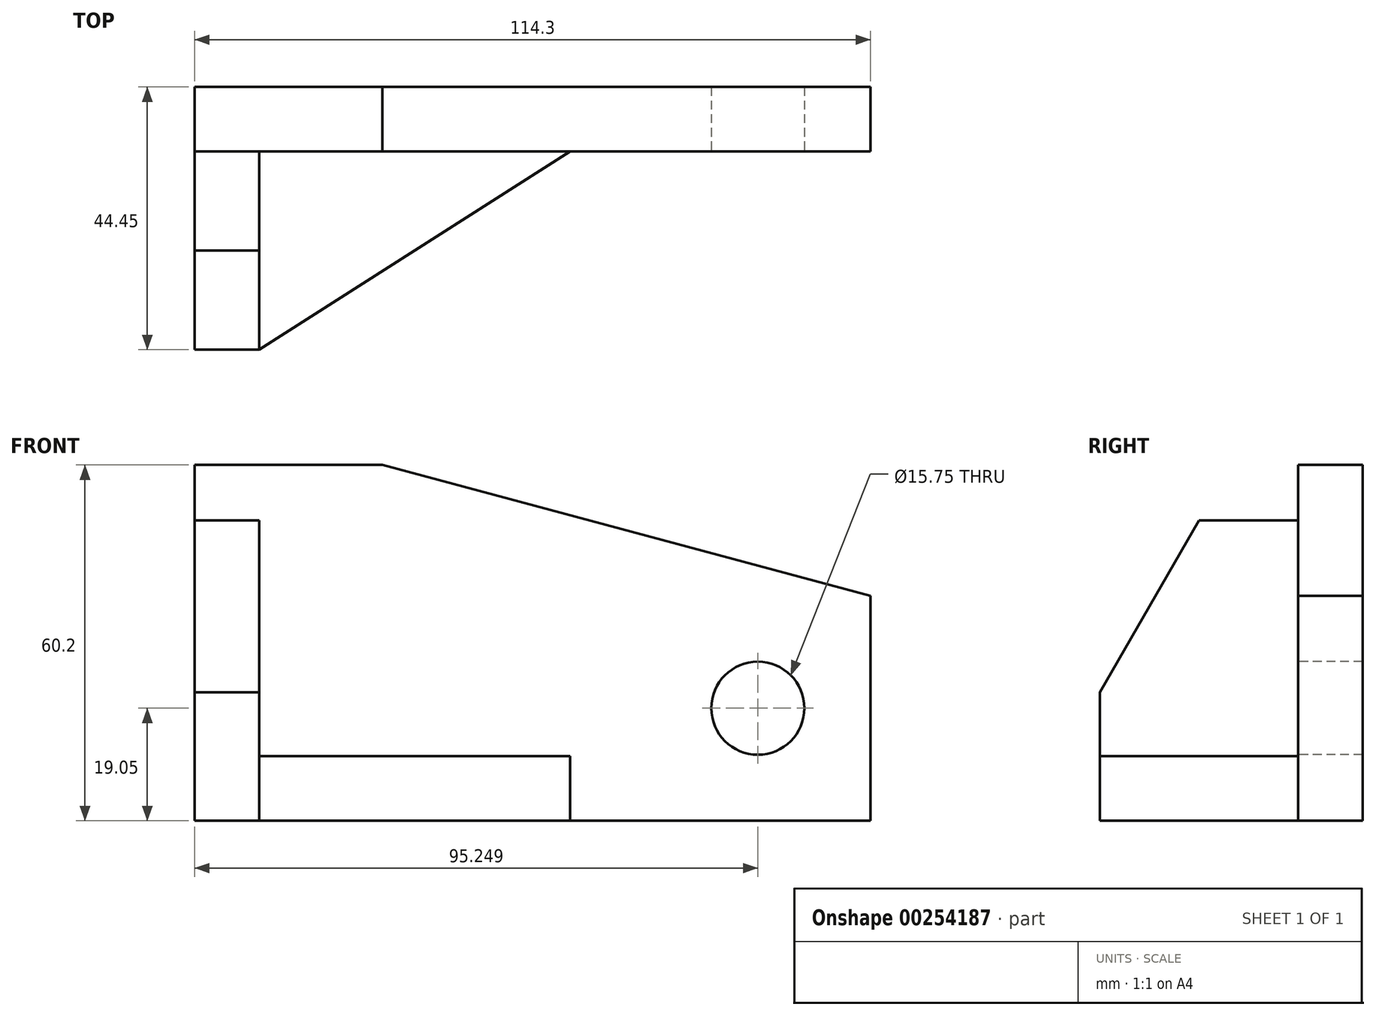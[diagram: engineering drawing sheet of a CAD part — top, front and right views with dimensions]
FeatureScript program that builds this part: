
annotation { "Feature Type Name" : "Feature", "Feature Type Description" : "" }
export const myFeature = defineFeature(function(context is Context, id is Id, definition is map)
    precondition{}
    {
        {
            var Q0;
            Q0=qCreatedBy(makeId("Top.planeOp"),FACE);
            var sketch = newSketch(context, id + "F0", { "sketchPlane" : qUnion([Q0])});
            skLineSegment(sketch, "E0", {"start": v(-49.98, 29.18) * mm, "end": v(64.32, 29.18) * mm});
            skLineSegment(sketch, "E1", {"start": v(-49.98, 29.18) * mm, "end": v(-49.98, 18.26) * mm});
            skLineSegment(sketch, "E2", {"start": v(-49.98, 18.26) * mm, "end": v(-49.98, -15.27) * mm});
            skLineSegment(sketch, "E3", {"start": v(-49.98, -15.27) * mm, "end": v(-39.06, -15.27) * mm});
            skLineSegment(sketch, "E4", {"start": v(-49.98, -15.27) * mm, "end": v(13.52, -15.27) * mm, "construction": true});
            skPoint(sketch, "E4.endSnap0", {"position": v(-44.52, -15.27) * mm});
            skLineSegment(sketch, "E5", {"start": v(-49.98, 18.26) * mm, "end": v(64.32, 18.26) * mm});
            skLineSegment(sketch, "E6", {"start": v(64.32, 18.26) * mm, "end": v(64.32, 29.18) * mm});
            skLineSegment(sketch, "E7", {"start": v(-39.06, -15.27) * mm, "end": v(-39.06, 18.26) * mm});
            skLineSegment(sketch, "E8", {"start": v(-39.06, -15.27) * mm, "end": v(13.52, 18.26) * mm});
            skLineSegment(sketch, "E9", {"start": v(-49.98, 29.18) * mm, "end": v(-18.23, 29.18) * mm});
            skLineSegment(sketch, "E10", {"start": v(-18.23, 29.18) * mm, "end": v(-18.23, 18.26) * mm});
            skSolve(sketch);
        }
        {
            var Q0;
            {var subQ3=sQuery(id+"F0.wireOp",EDGE,"E1");Q0=makeQuery(id+"F0.imprint","IMPRINT",FACE,{"disambiguationData":[TD([[makeQuery(id+"F0.imprint","IMPRINT",EDGE,{"derivedFrom":subQ3}),1.0]])]});}
            extrude(context, id + "F1", {"entities" : qUnion([Q0]), "depth" : 60.2 * mm});
        }
        {
            var Q0;
            Q0=makeQuery(id+"F0.imprint","IMPRINT",FACE,{"disambiguationData":[TD([[makeQuery(id+"F0.imprint","IMPRINT",EDGE,{"derivedFrom":sQuery(id+"F0.wireOp",EDGE,"E0")}),-1.0]])]});
            extrude(context, id + "F2", {"entities" : qUnion([Q0]), "operationType" : NewBodyOperationType.ADD, "depth" : 60.2 * mm});
        }
        {
            var Q0;
            Q0=makeQuery(id+"F2.opExtrude","CAP_EDGE",EDGE,{"disambiguationData":[OSD([sQuery(id+"F0.wireOp",EDGE,"E6")])],"isStart":false});
            chamfer(context, id + "F3", {"entities" : qUnion([Q0]), "chamferType" : ChamferType.OFFSET_ANGLE, "width" : 82.55 * mm, "oppositeDirection" : false, "angle" : 15 * degree, "tangentPropagation" : true});
        }
        {
            var Q0;
            {var subQ0=sQuery(id+"F0.wireOp",EDGE,"E5");Q0=makeQuery(id+"F2.boolean.opBoolean","MERGE",FACE,{"derivedFrom":[makeQuery(id+"F1.opExtrude","SWEPT_FACE",FACE,{"disambiguationData":[OSD([subQ0])]}),makeQuery(id+"F2.opExtrude","SWEPT_FACE",FACE,{"disambiguationData":[OSD([subQ0])]})]});}
            var sketch = newSketch(context, id + "F4", { "sketchPlane" : qUnion([Q0])});
            skLineSegment(sketch, "E11", {"start": v(-49.98, 0) * mm, "end": v(-49.98, 50.8) * mm});
            skLineSegment(sketch, "E12", {"start": v(-49.98, 0) * mm, "end": v(-39.06, 0) * mm});
            skLineSegment(sketch, "E13", {"start": v(-39.06, 0) * mm, "end": v(-39.06, 50.8) * mm});
            skLineSegment(sketch, "E14", {"start": v(-49.98, 50.8) * mm, "end": v(-39.06, 50.8) * mm});
            skLineSegment(sketch, "E15", {"start": v(-49.98, 0) * mm, "end": v(-49.98, 22.1) * mm});
            skLineSegment(sketch, "E16", {"start": v(-49.98, 22.1) * mm, "end": v(-39.06, 22.1) * mm});
            skLineSegment(sketch, "E17", {"start": v(64.32, 0) * mm, "end": v(45.27, 0) * mm});
            skLineSegment(sketch, "E18", {"start": v(45.27, 0) * mm, "end": v(45.27, 19.05) * mm});
            skCircle(sketch, "E19", {"center": v(45.27, 19.05) * mm, "radius": 7.87 * mm});
            skLineSegment(sketch, "E20.bottom", {"start": v(-18.23, 60.2) * mm, "end": v(64.32, 60.2) * mm});
            skSolve(sketch);
        }
        {
            var Q0;
            {var subQ0=sQuery(id+"F0.wireOp",EDGE,"E7");Q0=makeQuery(id+"F0.imprint","IMPRINT",FACE,{"disambiguationData":[TD([[makeQuery(id+"F0.imprint","IMPRINT",EDGE,{"derivedFrom":subQ0}),-1.0]])]});}
            extrude(context, id + "F5", {"entities" : qUnion([Q0]), "operationType" : NewBodyOperationType.ADD, "depth" : 10.92 * mm});
        }
        {
            var Q0;
            Q0=sQuery(id+"F4.wireOp",VERTEX,"E19.center");
            var Q1;
            Q1=makeQuery(id+"F1.opExtrude","SWEPT_BODY",BODY,{"disambiguationData":[OSD([sQuery(id+"F0.wireOp",EDGE,"E1"),sQuery(id+"F0.wireOp",EDGE,"E5"),sQuery(id+"F0.wireOp",EDGE,"E9"),sQuery(id+"F0.wireOp",EDGE,"E10")])]});
            hole(context, id + "F6", {"style" : HoleStyle.SIMPLE, "endStyle" : HoleEndStyle.THROUGH, "holeDiameter" : 15.75 * mm, "tappedDepth" : 12.7 * mm, "tapClearance" : 3, "locations" : qUnion([Q0]), "scope" : qUnion([Q1])});
        }
        {
            var Q0;
            Q0=makeQuery(id+"F4.imprint","IMPRINT",FACE,{"disambiguationData":[TD([[makeQuery(id+"F4.imprint","IMPRINT",EDGE,{"derivedFrom":sQuery(id+"F4.wireOp",EDGE,"E11")}),1.0]])]});
            extrude(context, id + "F7", {"entities" : qUnion([Q0]), "operationType" : NewBodyOperationType.ADD, "depth" : 33.53 * mm});
        }
        {
            var Q0;
            {var subQ0=sQuery(id+"F4.wireOp",EDGE,"E12");Q0=makeQuery(id+"F4.imprint","IMPRINT",FACE,{"disambiguationData":[TD([[makeQuery(id+"F4.imprint","IMPRINT",EDGE,{"derivedFrom":subQ0}),1.0]])]});}
            extrude(context, id + "F8", {"entities" : qUnion([Q0]), "operationType" : NewBodyOperationType.ADD, "depth" : 33.53 * mm});
        }
        {
            var Q0;
            Q0=makeQuery(id+"F7.opExtrude","CAP_EDGE",EDGE,{"disambiguationData":[OSD([sQuery(id+"F4.wireOp",EDGE,"E14")])],"isStart":false});
            chamfer(context, id + "F9", {"entities" : qUnion([Q0]), "chamferType" : ChamferType.OFFSET_ANGLE, "width" : 16.76 * mm, "oppositeDirection" : false, "angle" : 60 * degree, "tangentPropagation" : true});
        }
    });
